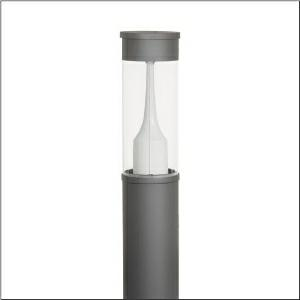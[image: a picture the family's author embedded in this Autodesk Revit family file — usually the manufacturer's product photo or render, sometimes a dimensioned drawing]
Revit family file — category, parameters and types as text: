
# Revit family: city-light_400_iq___p1_0a_5xa5305nf14h_7630
name_source: partatom
category: Lighting Fixtures
units: mm (PartAtom-declared; Revit-internal decimal feet)

## family parameters
Cut with Voids When Loaded = No
Host = Face
Light Source = No
Part Type = Normal
Room Calculation Point = No
Round Connector Dimension = Use Diameter
Shared = No

## types (1)
- --- (1 x LED, 1510 lm, 11.8 W, 2700K)
    Apparent Load = 12 VA
    CIE Flux Codes = 32 61 90 93 100
    Color Rendering = 70
    Color Temperature = 2700K
    Default Elevation = 1800 mm
    Description = City-Light 400 iQ, light pillar, Module 540 iQ-SR, primary light control with 3 zone facetted reflector, of plastic, silver coated, highly specular, structured, primary optical cover: cover, of PMMA, transparent, partly coated, light distribution: P1.0a, primary light characteristic: strongly asymmetric, LED, High Power LED, rated luminous flux: 1.510lm, luminous efficacy: 128lm/W, light colour: 727, colour temperature: 2700K, control gear: ECG iQ, control: presetting dimming logarithmic, Street-Remote, Auto-Match, Temp-Guard, Lumen-Switch, Night-Set, Smart-Wire, Light-Fading, Desk-Remote (wireless, voltage-free reading and setting of iQ features in the workshop via application-optimized NFC function/RFID function), optimised constant luminous flux control (CLO 2.0), with terminal, 6-pole, max. 2.5mm², mains connection: 220..240V, AC, 50/60Hz, start of lifetime: 12W, end of lifetime: 12W, reduction: 6W, luminaire housing, cylindrical, of extruded aluminium section, coated, Siteco® metallic grey (DB 702S), length: 4.694mm, diameter: 200mm, Module 540 iQ-SR, traffic white (RAL 9016), equipment: standard, protection rating (complete): IP65, insulation class (complete): insulation class II (safety insulation), certification: CE, ENEC, VDE, packaging unit: 1 piece

Light Distribution: P1.0a
    Height = 500 mm
    Lamp = 1 x LED
    Lamp Light Flux = 1510 lm
    Lamp Power = 11.8 W
    Lamp count = 1
    Length = 200 mm
    Luminous efficacy = 128 lm/W
    Manufacturer = Siteco
    ModVariant = No
    Model = 5XA5305NF14H
    Mounting Place = Floor
    Mounting Type = Freestanding
    Number of Poles = 1
    OnlyDefault = Yes
    Power Factor = 1
    Product Name = City-Light 400 iQ | P1.0a
    Product group = light pillar | freestanding
    ProductGroupID = 1301
    Protection Class = Protection class II
    Protection Degree = IP 65
    RLX_Detail_Level = 1
    RlxData = <blob elided: 75233 chars, md5=72142594>
    Socket = socket
    Standby Power = 0 W
    System Light Flux = 1510 lm
    System Power = 12 W
    Type Comments = factory setting: luminous flux: 100 % | dim-lin: 254 | 472 mA
    Type Image = l_1006914.jpg
    URL = http://relux.com
    VarID = @adj_062961
    Voltage = 0 V
    Weight = 0.00 kg
    Width = 0 mm  [stored 0 ft]

note: [stored X ft] marks values corroborated as IEEE doubles in the binary element streams (Revit-internal decimal feet)

## geometry (parser evidence)
native form markers: Blend x4, Sweep x10
no freeform markers — native parametric forms only
